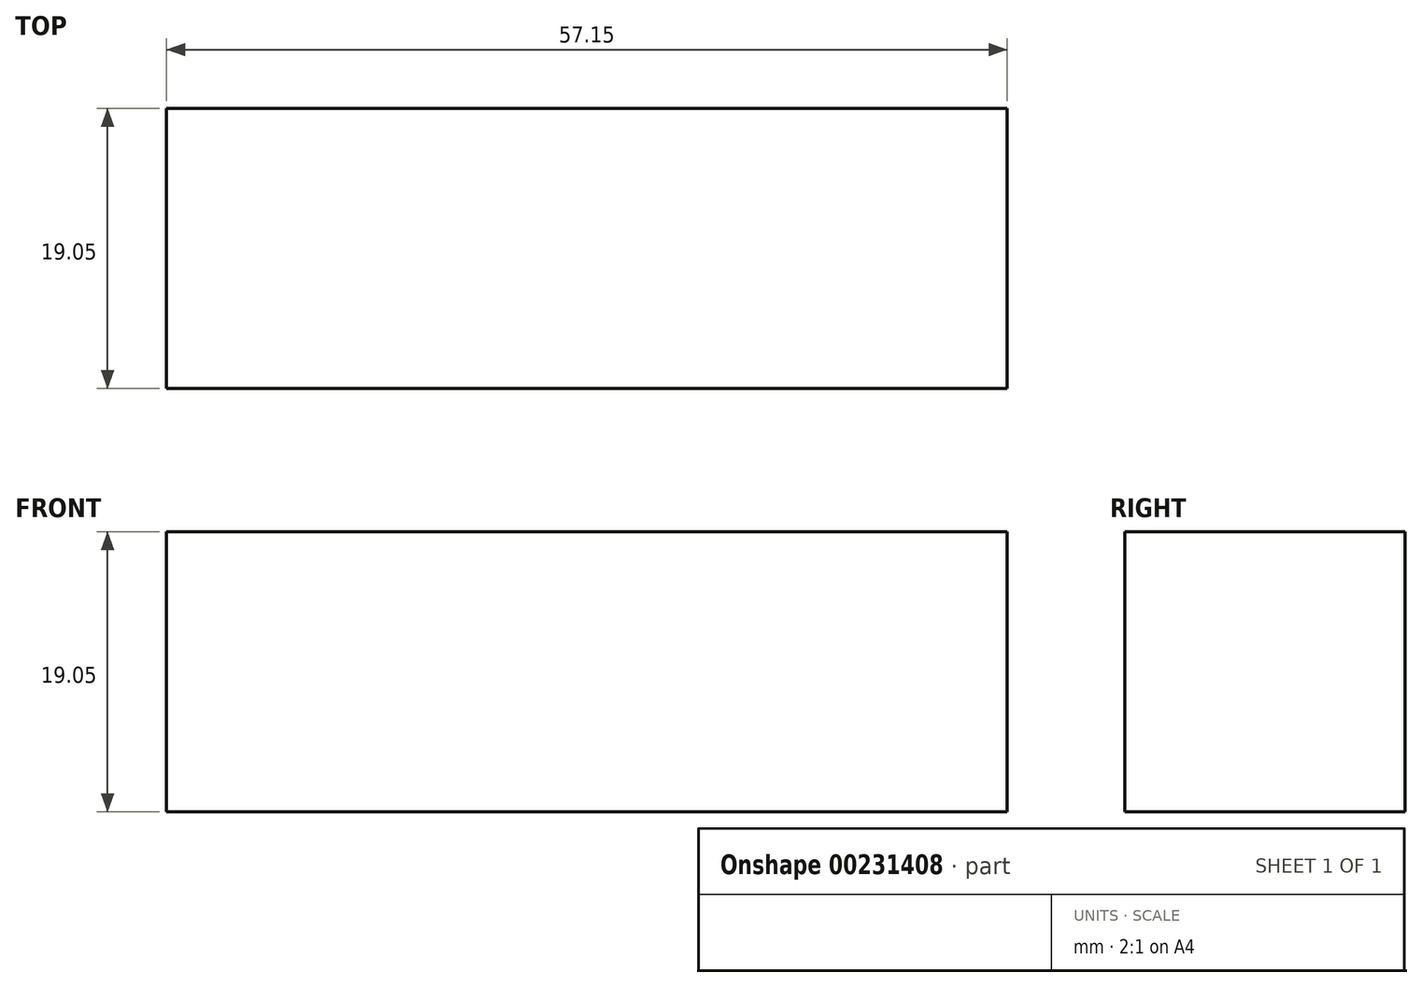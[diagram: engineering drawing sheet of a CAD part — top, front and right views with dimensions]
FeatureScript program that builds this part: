
annotation { "Feature Type Name" : "Feature", "Feature Type Description" : "" }
export const myFeature = defineFeature(function(context is Context, id is Id, definition is map)
    precondition{}
    {
        {
            var Q0;
            Q0=qCreatedBy(makeId("Front.planeOp"),FACE);
            var sketch = newSketch(context, id + "F0", { "sketchPlane" : qUnion([Q0])});
            skLineSegment(sketch, "E0.bottom", {"start": v(-16.69, 39.53) * mm, "end": v(40.46, 39.53) * mm});
            skLineSegment(sketch, "E0.top", {"start": v(-16.69, 20.48) * mm, "end": v(40.46, 20.48) * mm});
            skLineSegment(sketch, "E0.left", {"start": v(-16.69, 39.53) * mm, "end": v(-16.69, 20.48) * mm});
            skLineSegment(sketch, "E0.right", {"start": v(40.46, 39.53) * mm, "end": v(40.46, 20.48) * mm});
            skSolve(sketch);
        }
        {
            var Q0;
            Q0 = qSketchRegion(id + "F0", true);
            extrude(context, id + "F1", {"entities" : qUnion([Q0]), "depth" : 19.05 * mm});
        }
    });
